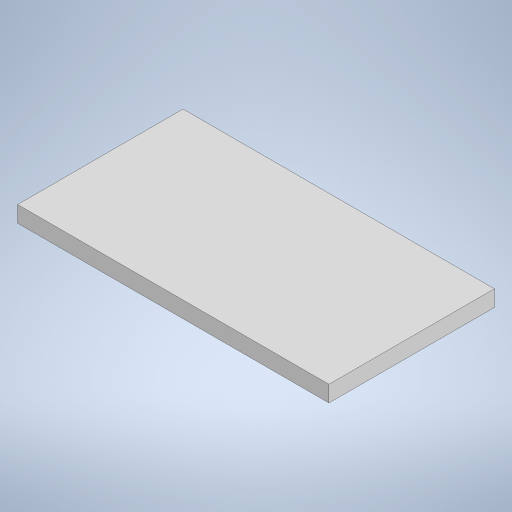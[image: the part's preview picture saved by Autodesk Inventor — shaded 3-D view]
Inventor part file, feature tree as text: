
AUTODESK INVENTOR PART (.ipt)
format: ipt  version: 2023 (Build 270158000, 158)  size: 200,192 bytes
history: native  units: in
note: dims shown in document units (in); Inventor stores cm internally (conversion verified against a paired STEP export)
features: extrude x1, sketch x1
ambient origin geometry x8: Origin, YZ Plane, XZ Plane, XY Plane, X Axis, Y Axis, Z Axis, Center Point
bodies: Solid1 (feature_tree)
feature tree (2):
  extrude  "Extrusion1"  Depth=1.275in
  sketch  "Sketch1"  dims[d0=2.4in d1=1.275in d2=0.125in d3=0.0in]
